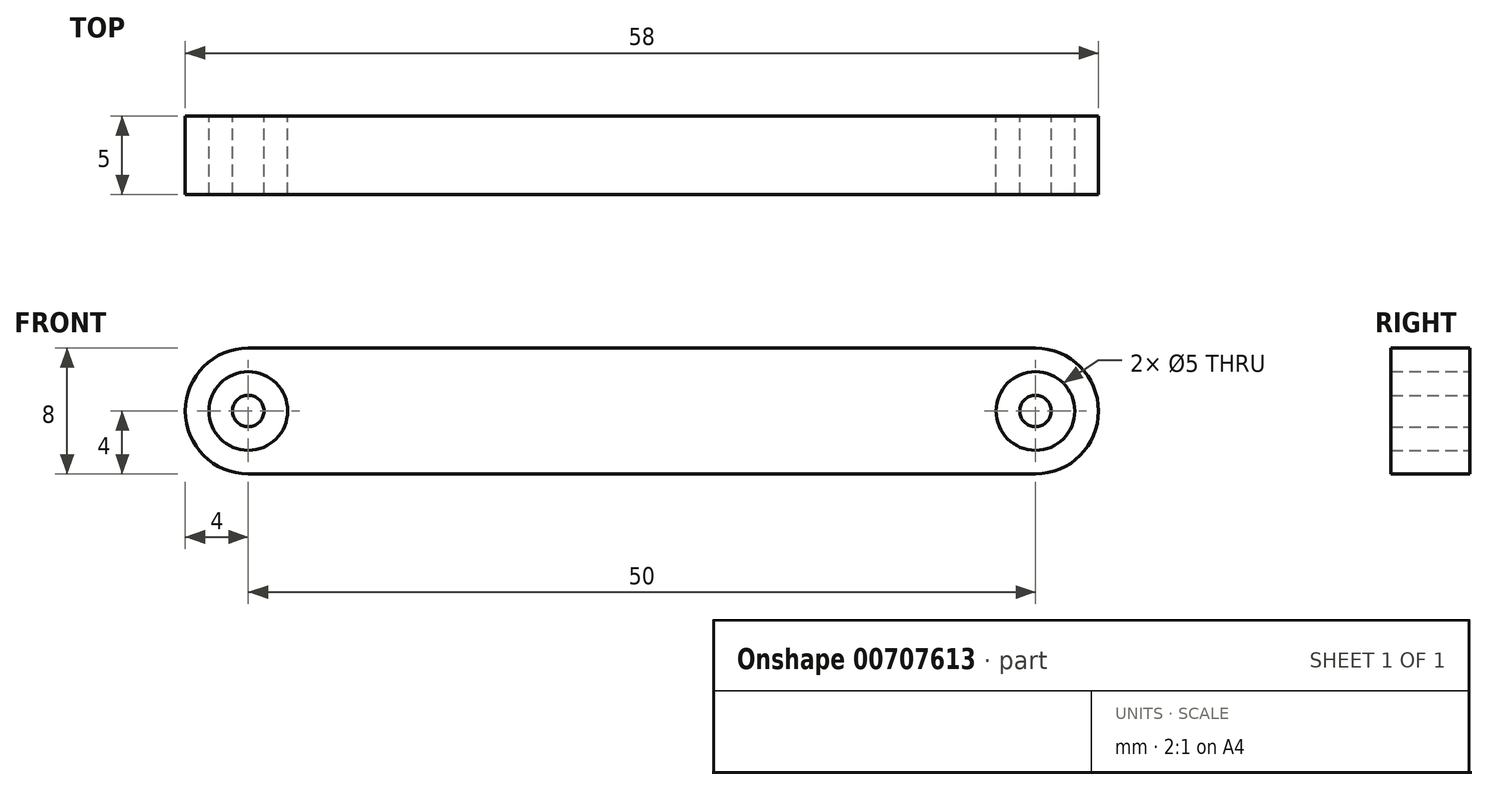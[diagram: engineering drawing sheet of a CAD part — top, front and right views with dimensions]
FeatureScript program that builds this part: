
annotation { "Feature Type Name" : "Feature", "Feature Type Description" : "" }
export const myFeature = defineFeature(function(context is Context, id is Id, definition is map)
    precondition{}
    {
        {
            var Q0;
            Q0=qCreatedBy(makeId("Front.planeOp"),FACE);
            var sketch = newSketch(context, id + "F0", { "sketchPlane" : qUnion([Q0])});
            skCircle(sketch, "E0", {"center": v(0, 0) * mm, "radius": 1 * mm});
            skArc(sketch, "E1", {"start": v(0, 4) * mm, "mid": v(-4, 0) * mm, "end": v(0, -4) * mm});
            skCircle(sketch, "E2", {"center": v(0, 0) * mm, "radius": 2.5 * mm});
            skLineSegment(sketch, "E3", {"start": v(0, 0) * mm, "end": v(50, 0) * mm});
            skArc(sketch, "E4", {"start": v(50, -4) * mm, "mid": v(54, 0) * mm, "end": v(50, 4) * mm});
            skCircle(sketch, "E5", {"center": v(50, 0) * mm, "radius": 2.5 * mm});
            skCircle(sketch, "E6", {"center": v(50, 0) * mm, "radius": 1 * mm});
            skLineSegment(sketch, "E7", {"start": v(0, -4) * mm, "end": v(50, -4) * mm});
            skLineSegment(sketch, "E8", {"start": v(0, 4) * mm, "end": v(50, 4) * mm});
            skSolve(sketch);
        }
        {
            var Q0;
            Q0=makeQuery(id+"F0.imprint","IMPRINT",FACE,{"disambiguationData":[TD([[makeQuery(id+"F0.imprint","IMPRINT",EDGE,{"derivedFrom":sQuery(id+"F0.wireOp",EDGE,"E0")}),1.0]])]});
            var Q1;
            Q1=makeQuery(id+"F0.imprint","IMPRINT",FACE,{"disambiguationData":[TD([[makeQuery(id+"F0.imprint","IMPRINT",EDGE,{"derivedFrom":sQuery(id+"F0.wireOp",EDGE,"E1")}),1.0]])]});
            var Q2;
            Q2=makeQuery(id+"F0.imprint","IMPRINT",FACE,{"disambiguationData":[TD([[makeQuery(id+"F0.imprint","IMPRINT",EDGE,{"derivedFrom":sQuery(id+"F0.wireOp",EDGE,"E6")}),1.0]])]});
            extrude(context, id + "F1", {"entities" : qUnion([Q0, Q1, Q2]), "depth" : 5 * mm, "offsetDistance" : 25.4 * mm});
        }
    });
